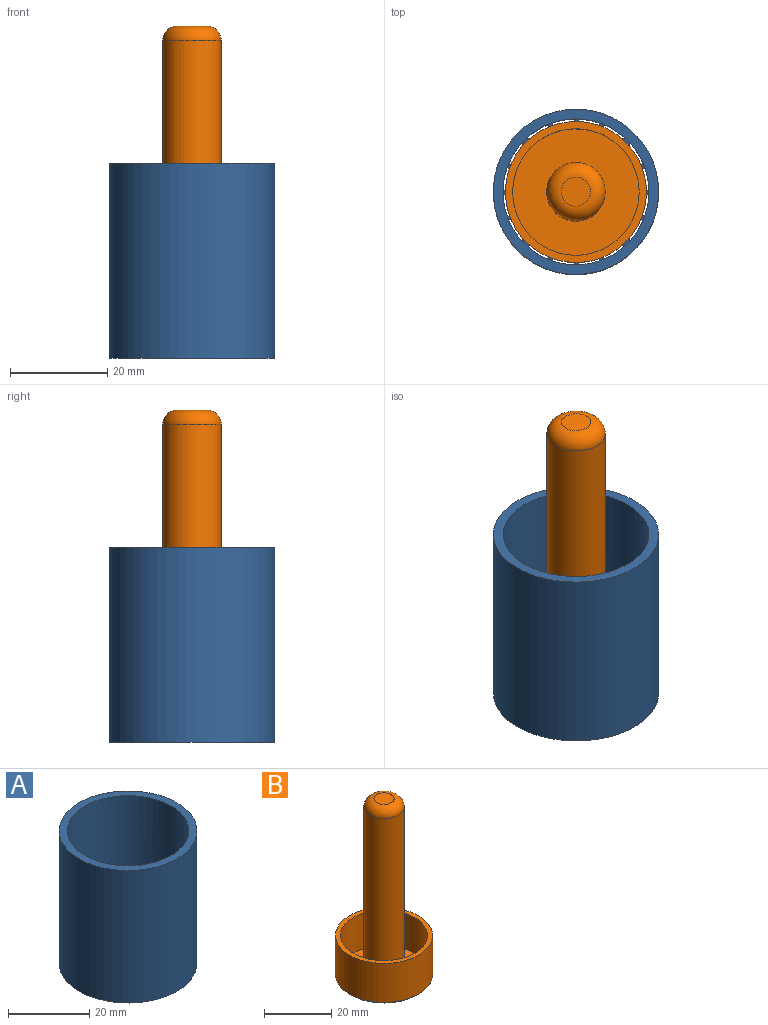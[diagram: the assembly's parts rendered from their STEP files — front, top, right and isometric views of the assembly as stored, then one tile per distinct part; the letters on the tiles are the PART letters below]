
ASSEMBLY  parts=2 mates=1
PART A: 113 faces, bbox 34x34x40 mm
  f0: plane 34x34mm, normal (0,0,-1), area 392mm2, adj f1,f2,f3,f4,f5,f6,f7,f8
  f1: cylinder r=15mm len=40mm, axis (0,0,-1), area 3755.2mm2, adj f0,f41,f42,f43,f44,f45,f46,f47
  f2: cylinder r=17mm len=40mm, axis (0,0,-1), area 4272.6mm2, adj f0,f49
  f3: plane 4.5x1mm, normal (-1,0,0), area 4.5mm2, adj f0,f50,f103,f112
  f4: plane 4.5x1mm, normal (1,0,0), area 4.5mm2, adj f0,f50,f100,f111
  f5: plane 4.5x1mm, normal (-1,0,0), area 4.5mm2, adj f0,f50,f100,f111
  f6: plane 4.5x1mm, normal (1,0,0), area 4.5mm2, adj f0,f50,f98,f109
  f7: plane 4.5x1mm, normal (-1,0,0), area 4.5mm2, adj f0,f50,f98,f109
  f8: plane 4.5x1mm, normal (1,0,0), area 4.5mm2, adj f0,f50,f96,f107
  f9: plane 4.5x1mm, normal (-1,0,0), area 4.5mm2, adj f0,f50,f96,f107
  f10: plane 4.5x1mm, normal (1,0,0), area 4.5mm2, adj f0,f50,f94,f104
  f11: plane 4.5x1mm, normal (-1,0,0), area 4.5mm2, adj f0,f50,f94,f104
  f12: plane 4.5x1mm, normal (-1,0,0), area 4.5mm2, adj f0,f50,f91,f102
  f13: plane 4.5x1mm, normal (1,0,0), area 4.5mm2, adj f0,f50,f88,f101
  f14: plane 4.5x1mm, normal (-1,0,0), area 4.5mm2, adj f0,f50,f88,f101
  f15: plane 4.5x1mm, normal (1,0,0), area 4.5mm2, adj f0,f50,f86,f99
  f16: plane 4.5x1mm, normal (-1,0,0), area 4.5mm2, adj f0,f50,f86,f99
  f17: plane 4.5x1mm, normal (1,0,0), area 4.5mm2, adj f0,f50,f84,f97
  f18: plane 4.5x1mm, normal (-1,0,0), area 4.5mm2, adj f0,f50,f84,f97
  f19: plane 4.5x1mm, normal (1,0,0), area 4.5mm2, adj f0,f50,f82,f95
  f20: plane 4.5x1mm, normal (-1,0,0), area 4.5mm2, adj f0,f50,f82,f95
  f21: plane 4.5x1mm, normal (1,0,0), area 4.5mm2, adj f0,f50,f80,f93
  f22: plane 4.5x1mm, normal (-1,0,0), area 4.5mm2, adj f0,f50,f79,f90
  f23: plane 4.5x1mm, normal (1,0,0), area 4.5mm2, adj f0,f50,f76,f89
  f24: plane 4.5x1mm, normal (-1,0,0), area 4.5mm2, adj f0,f50,f76,f89
  f25: plane 4.5x1mm, normal (1,0,0), area 4.5mm2, adj f0,f50,f74,f87
  f26: plane 4.5x1mm, normal (-1,0,0), area 4.5mm2, adj f0,f50,f74,f87
  f27: plane 4.5x1mm, normal (1,0,0), area 4.5mm2, adj f0,f50,f72,f85
  f28: plane 4.5x1mm, normal (-1,0,0), area 4.5mm2, adj f0,f50,f72,f85
  f29: plane 4.5x1mm, normal (1,0,0), area 4.5mm2, adj f0,f50,f70,f83
  f30: plane 4.5x1mm, normal (-1,0,0), area 4.5mm2, adj f0,f50,f70,f83
  f31: plane 4.5x1mm, normal (1,0,0), area 4.5mm2, adj f0,f50,f68,f81
  f32: plane 4.5x1mm, normal (-1,0,0), area 4.5mm2, adj f0,f50,f67,f78
  f33: plane 4.5x1mm, normal (1,0,0), area 4.5mm2, adj f0,f50,f65,f77
  f34: plane 4.5x1mm, normal (-1,0,0), area 4.5mm2, adj f0,f50,f65,f77
  f35: plane 4.5x1mm, normal (1,0,0), area 4.5mm2, adj f0,f50,f63,f75
  f36: plane 4.5x1mm, normal (-1,0,0), area 4.5mm2, adj f0,f50,f63,f75
  f37: plane 4.5x1mm, normal (1,0,0), area 4.5mm2, adj f0,f50,f61,f73
  f38: plane 4.5x1mm, normal (-1,0,0), area 4.5mm2, adj f0,f50,f61,f73
  f39: plane 4.5x1mm, normal (1,0,0), area 4.5mm2, adj f0,f50,f59,f71
  f40: plane 4.5x1mm, normal (-1,0,0), area 4.5mm2, adj f0,f50,f59,f71
  f41: plane 4.48x1mm, normal (1,0,0), area 4.5mm2, adj f0,f1,f50,f69
  f42: plane 1x0.04mm, normal (1,0,0), area 0mm2, adj f0,f1,f50,f66
  f43: plane 2.9x1mm, normal (-1,0,0), area 2.9mm2, adj f0,f1,f50,f66
  f44: plane 3.2x1mm, normal (1,0,0), area 3.2mm2, adj f0,f1,f50,f64
  f45: plane 4.01x1mm, normal (-1,0,0), area 4mm2, adj f0,f1,f50,f64
  f46: plane 4x1mm, normal (1,0,0), area 4mm2, adj f0,f1,f50,f62
  f47: plane 3.18x1mm, normal (-1,0,0), area 3.2mm2, adj f0,f1,f50,f62
  f48: plane 2.87x1mm, normal (1,0,0), area 2.9mm2, adj f0,f1,f50,f60
  f49: plane 34x34mm, normal (0,0,1), area 201.1mm2, adj f1,f2
  f50: plane 30x30mm, normal (0,0,1), area 190.9mm2, adj f1,f3,f4,f5,f6,f7,f8,f9
  f51: plane 1x0.02mm, normal (1,0,0), area 0mm2, adj f0,f1,f50,f110
  f52: plane 2.88x1mm, normal (-1,0,0), area 2.9mm2, adj f0,f1,f50,f110
  f53: plane 3.18x1mm, normal (1,0,0), area 3.2mm2, adj f0,f1,f50,f108
  f54: plane 3.99x1mm, normal (-1,0,0), area 4mm2, adj f0,f1,f50,f108
  f55: plane 3.98x1mm, normal (1,0,0), area 4mm2, adj f0,f1,f50,f106
  f56: plane 3.16x1mm, normal (-1,0,0), area 3.2mm2, adj f0,f1,f50,f106
  f57: plane 2.85x1mm, normal (1,0,0), area 2.9mm2, adj f0,f1,f50,f105
  f58: plane 4.46x1mm, normal (1,0,0), area 4.5mm2, adj f0,f1,f50,f92
  f59: plane 4.5x1mm, normal (0,1,0), area 4.5mm2, adj f0,f39,f40,f50
  f60: plane 4.48x1mm, normal (0,-1,0), area 4.5mm2, adj f0,f1,f48,f50
  f61: plane 4.5x1mm, normal (0,1,0), area 4.5mm2, adj f0,f37,f38,f50
  f62: plane 4.5x1mm, normal (0,-1,0), area 4.5mm2, adj f0,f46,f47,f50
  f63: plane 4.5x1mm, normal (0,1,0), area 4.5mm2, adj f0,f35,f36,f50
  f64: plane 4.5x1mm, normal (0,-1,0), area 4.5mm2, adj f0,f44,f45,f50
  f65: plane 4.5x1mm, normal (0,1,0), area 4.5mm2, adj f0,f33,f34,f50
  f66: plane 4.5x1mm, normal (0,-1,0), area 4.5mm2, adj f0,f42,f43,f50
  f67: plane 1x0.04mm, normal (0,1,0), area 0mm2, adj f0,f1,f32,f50
  f68: plane 3.15x1mm, normal (0,1,0), area 3.2mm2, adj f0,f1,f31,f50
  f69: plane 2.85x1mm, normal (0,-1,0), area 2.8mm2, adj f0,f1,f41,f50
  f70: plane 4.5x1mm, normal (0,1,0), area 4.5mm2, adj f0,f29,f30,f50
  f71: plane 4.5x1mm, normal (0,-1,0), area 4.5mm2, adj f0,f39,f40,f50
  f72: plane 4.5x1mm, normal (0,1,0), area 4.5mm2, adj f0,f27,f28,f50
  f73: plane 4.5x1mm, normal (0,-1,0), area 4.5mm2, adj f0,f37,f38,f50
  f74: plane 4.5x1mm, normal (0,1,0), area 4.5mm2, adj f0,f25,f26,f50
  f75: plane 4.5x1mm, normal (0,-1,0), area 4.5mm2, adj f0,f35,f36,f50
  f76: plane 4.5x1mm, normal (0,1,0), area 4.5mm2, adj f0,f23,f24,f50
  f77: plane 4.5x1mm, normal (0,-1,0), area 4.5mm2, adj f0,f33,f34,f50
  f78: plane 2.91x1mm, normal (0,-1,0), area 2.9mm2, adj f0,f1,f32,f50
  f79: plane 3.22x1mm, normal (0,1,0), area 3.2mm2, adj f0,f1,f22,f50
  f80: plane 3.96x1mm, normal (0,1,0), area 4mm2, adj f0,f1,f21,f50
  f81: plane 3.96x1mm, normal (0,-1,0), area 4mm2, adj f0,f1,f31,f50
  f82: plane 4.5x1mm, normal (0,1,0), area 4.5mm2, adj f0,f19,f20,f50
  f83: plane 4.5x1mm, normal (0,-1,0), area 4.5mm2, adj f0,f29,f30,f50
  f84: plane 4.5x1mm, normal (0,1,0), area 4.5mm2, adj f0,f17,f18,f50
  f85: plane 4.5x1mm, normal (0,-1,0), area 4.5mm2, adj f0,f27,f28,f50
  f86: plane 4.5x1mm, normal (0,1,0), area 4.5mm2, adj f0,f15,f16,f50
  f87: plane 4.5x1mm, normal (0,-1,0), area 4.5mm2, adj f0,f25,f26,f50
  f88: plane 4.5x1mm, normal (0,1,0), area 4.5mm2, adj f0,f13,f14,f50
  f89: plane 4.5x1mm, normal (0,-1,0), area 4.5mm2, adj f0,f23,f24,f50
  f90: plane 4.03x1mm, normal (0,-1,0), area 4mm2, adj f0,f1,f22,f50
  f91: plane 4.03x1mm, normal (0,1,0), area 4mm2, adj f0,f1,f12,f50
  f92: plane 2.84x1mm, normal (0,1,0), area 2.8mm2, adj f0,f1,f50,f58
  f93: plane 3.14x1mm, normal (0,-1,0), area 3.1mm2, adj f0,f1,f21,f50
  f94: plane 4.5x1mm, normal (0,1,0), area 4.5mm2, adj f0,f10,f11,f50
  f95: plane 4.5x1mm, normal (0,-1,0), area 4.5mm2, adj f0,f19,f20,f50
  f96: plane 4.5x1mm, normal (0,1,0), area 4.5mm2, adj f0,f8,f9,f50
  f97: plane 4.5x1mm, normal (0,-1,0), area 4.5mm2, adj f0,f17,f18,f50
  f98: plane 4.5x1mm, normal (0,1,0), area 4.5mm2, adj f0,f6,f7,f50
  f99: plane 4.5x1mm, normal (0,-1,0), area 4.5mm2, adj f0,f15,f16,f50
  f100: plane 4.5x1mm, normal (0,1,0), area 4.5mm2, adj f0,f4,f5,f50
  f101: plane 4.5x1mm, normal (0,-1,0), area 4.5mm2, adj f0,f13,f14,f50
  f102: plane 3.21x1mm, normal (0,-1,0), area 3.2mm2, adj f0,f1,f12,f50
  f103: plane 2.91x1mm, normal (0,1,0), area 2.9mm2, adj f0,f1,f3,f50
  f104: plane 4.5x1mm, normal (0,-1,0), area 4.5mm2, adj f0,f10,f11,f50
  f105: plane 4.46x1mm, normal (0,1,0), area 4.5mm2, adj f0,f1,f50,f57
  f106: plane 4.5x1mm, normal (0,1,0), area 4.5mm2, adj f0,f50,f55,f56
  f107: plane 4.5x1mm, normal (0,-1,0), area 4.5mm2, adj f0,f8,f9,f50
  f108: plane 4.5x1mm, normal (0,1,0), area 4.5mm2, adj f0,f50,f53,f54
  f109: plane 4.5x1mm, normal (0,-1,0), area 4.5mm2, adj f0,f6,f7,f50
  f110: plane 4.5x1mm, normal (0,1,0), area 4.5mm2, adj f0,f50,f51,f52
  f111: plane 4.5x1mm, normal (0,-1,0), area 4.5mm2, adj f0,f4,f5,f50
  f112: plane 1x0.02mm, normal (0,-1,0), area 0mm2, adj f0,f1,f3,f50
PART B: 9 faces, bbox 29x29x65 mm
  f0: cylinder r=14.5mm len=29mm, axis (0,0,-1), area 1293.7mm2, adj f3,f8
  f1: plane 27.4x27.4mm, normal (0,0,-1), area 589.6mm2, adj f8
  f2: cylinder r=13mm len=26mm, axis (0,0,-1), area 1061.9mm2, adj f3,f4
  f3: plane 29x29mm, normal (0,0,1), area 129.6mm2, adj f0,f2
  f4: plane 26x26mm, normal (0,0,1), area 417.8mm2, adj f2,f5
  f5: cylinder r=6mm len=60mm, axis (0,0,-1), area 2261.9mm2, adj f4,f7
  f6: plane 6x6mm, normal (0,0,1), area 28.3mm2, adj f7
  f7: torus R=3mm, axis (0,0,1), area 145.4mm2, adj f5,f6
  f8: cone r=14.5mm half-angle=45deg, axis (0,0,1), area 100.2mm2, adj f0,f1
PLACE A t=(-7.44,-11.4,-53.36)mm fixed
PLACE B t=(-7.44,-11.4,-50.09)mm
MATE slider A.f1 <-> B.f0  axis (0,0,-1) through (-7.44,-11.4,-13.36)mm
